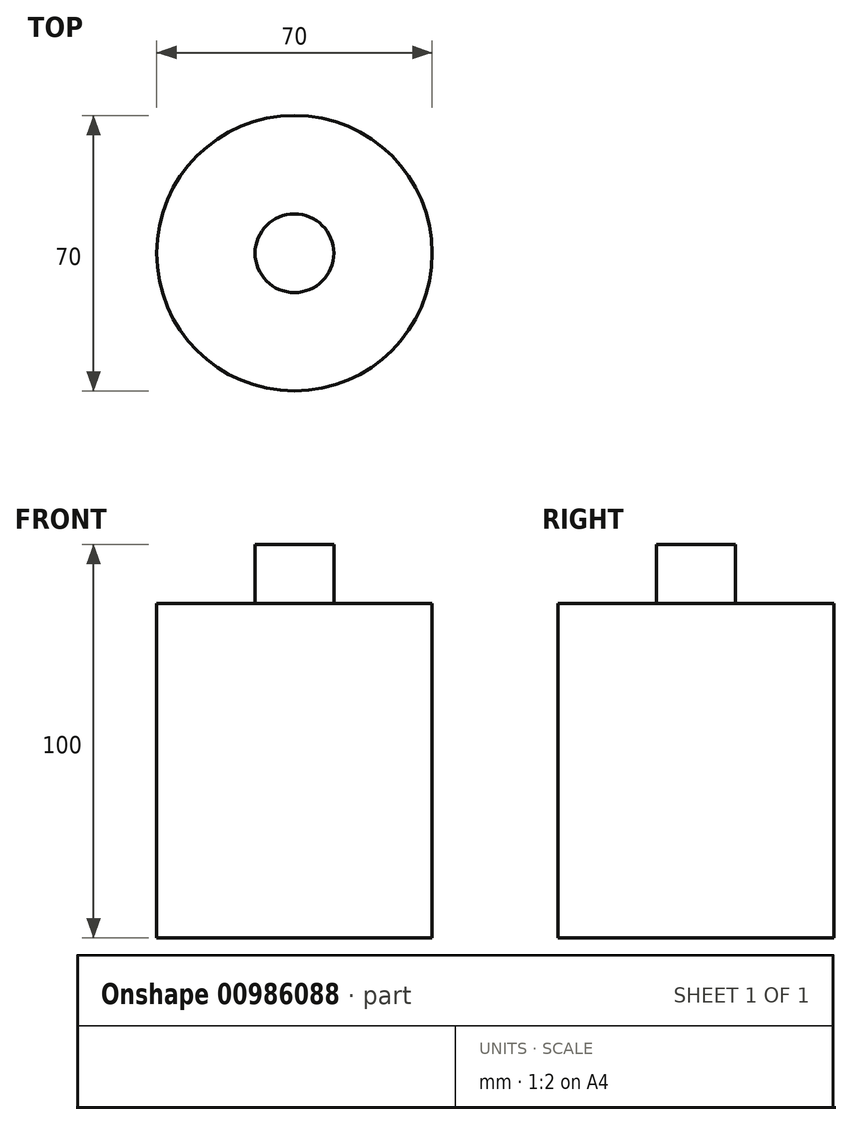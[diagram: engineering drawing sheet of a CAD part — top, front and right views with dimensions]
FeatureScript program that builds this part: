
annotation { "Feature Type Name" : "Feature", "Feature Type Description" : "" }
export const myFeature = defineFeature(function(context is Context, id is Id, definition is map)
    precondition{}
    {
        {
            var Q0;
            Q0=qCreatedBy(makeId("Front.planeOp"),FACE);
            var sketch = newSketch(context, id + "F0", { "sketchPlane" : qUnion([Q0])});
            skLineSegment(sketch, "E0", {"start": v(0, 50) * mm, "end": v(10, 50) * mm});
            skLineSegment(sketch, "E1", {"start": v(10, 50) * mm, "end": v(10, 35) * mm});
            skLineSegment(sketch, "E2", {"start": v(0, -50) * mm, "end": v(35, -50) * mm});
            skLineSegment(sketch, "E3", {"start": v(10, 35) * mm, "end": v(35, 35) * mm});
            skLineSegment(sketch, "E4", {"start": v(35, 35) * mm, "end": v(35, -50) * mm});
            skLineSegment(sketch, "E5", {"start": v(0, 50) * mm, "end": v(0, -50) * mm});
            skSolve(sketch);
        }
        {
            var Q0;
            Q0 = qSketchRegion(id + "F0", true);
            var Q1;
            Q1=sQuery(id+"F0.wireOp",EDGE,"E5");
            revolve(context, id + "F1", {"surfaceOperationType" : NewSurfaceOperationType.NEW, "entities" : qUnion([Q0]), "axis" : qUnion([Q1]), "revolveType" : RevolveType.FULL});
        }
    });
